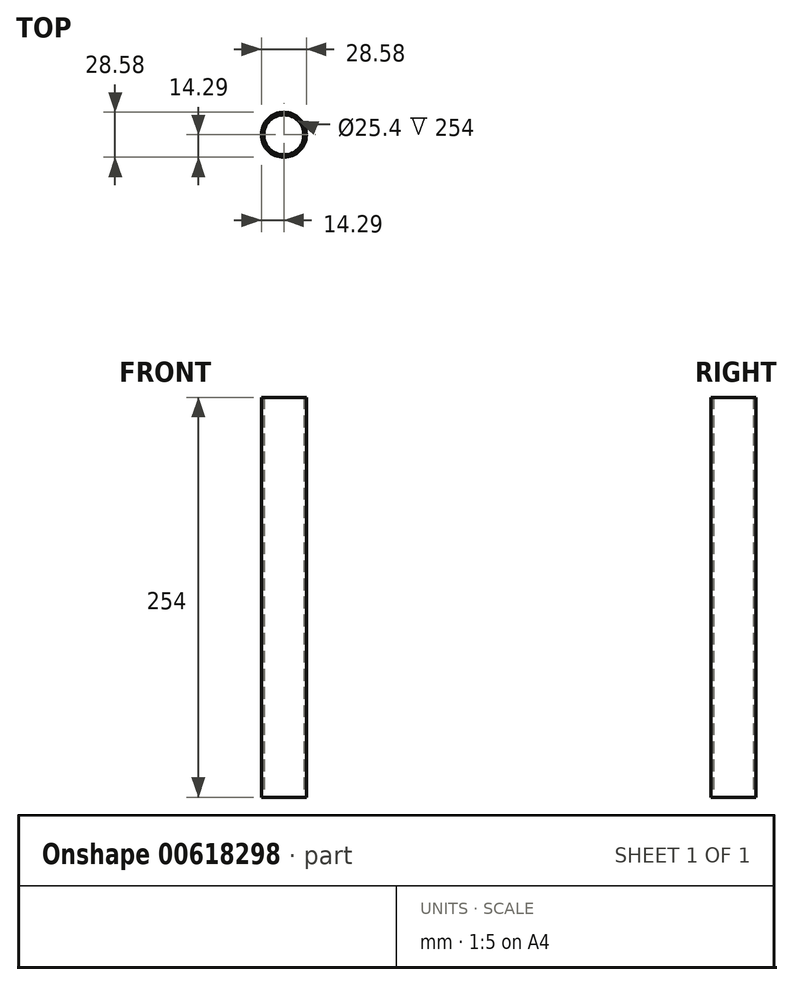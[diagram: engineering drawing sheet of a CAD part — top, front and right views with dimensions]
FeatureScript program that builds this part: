
annotation { "Feature Type Name" : "Feature", "Feature Type Description" : "" }
export const myFeature = defineFeature(function(context is Context, id is Id, definition is map)
    precondition{}
    {
        {
            var Q0;
            Q0=qCreatedBy(makeId("Top.planeOp"),FACE);
            var sketch = newSketch(context, id + "F0", { "sketchPlane" : qUnion([Q0])});
            skLineSegment(sketch, "E0", {"start": v(0, 0) * mm, "end": v(12.7, 0) * mm});
            skCircle(sketch, "E1", {"center": v(0, 0) * mm, "radius": 12.7 * mm});
            skCircle(sketch, "E2.0", {"center": v(0, 0) * mm, "radius": 14.29 * mm});
            skSolve(sketch);
        }
        {
            var Q0;
            Q0=qCreatedBy(makeId("Top.planeOp"),FACE);
            var sketch = newSketch(context, id + "F1", { "sketchPlane" : qUnion([Q0])});
            skSolve(sketch);
        }
        {
            var Q0;
            Q0=qSketchRegion(id+"F1",true);
            var Q1;
            Q1=makeQuery(id+"F0.imprint","IMPRINT",FACE,{"disambiguationData":[TD([[makeQuery(id+"F0.imprint","IMPRINT",EDGE,{"derivedFrom":sQuery(id+"F0.wireOp",EDGE,"E1")}),-1.0]])]});
            extrude(context, id + "F2", {"entities" : qUnion([Q0, Q1]), "depth" : 254 * mm, "offsetDistance" : 25.4 * mm});
        }
    });
